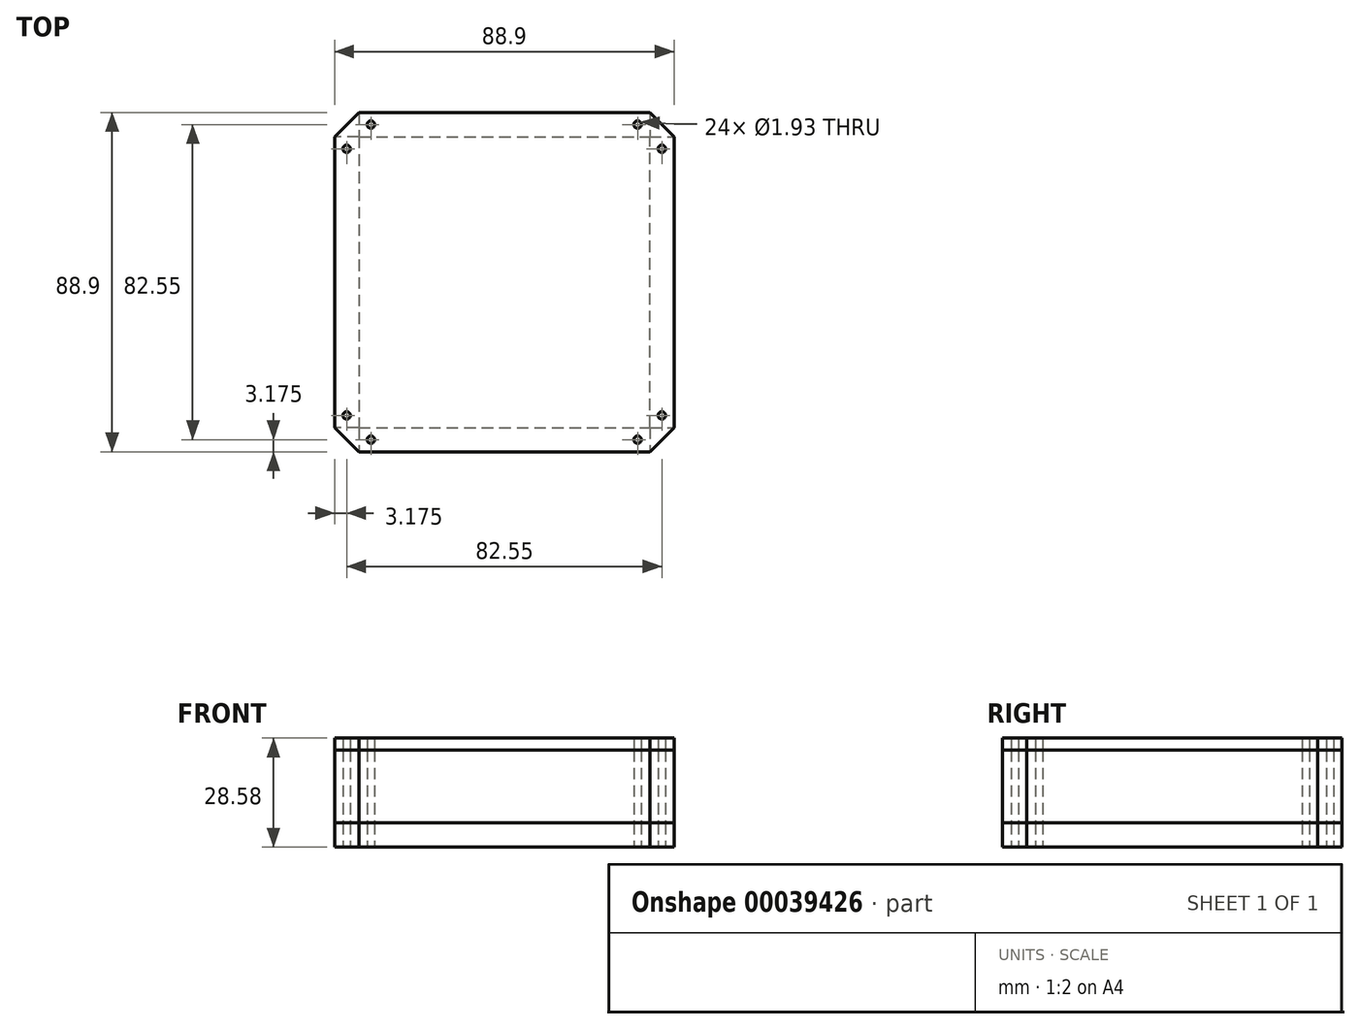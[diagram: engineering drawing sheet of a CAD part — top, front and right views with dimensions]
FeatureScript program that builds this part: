
annotation { "Feature Type Name" : "Feature", "Feature Type Description" : "" }
export const myFeature = defineFeature(function(context is Context, id is Id, definition is map)
    precondition{}
    {
        {
            var Q0;
            Q0=qCreatedBy(makeId("Top.planeOp"),FACE);
            var sketch = newSketch(context, id + "F0", { "sketchPlane" : qUnion([Q0])});
            skLineSegment(sketch, "E0.rect.bottom", {"start": v(-38.1, 44.45) * mm, "end": v(38.1, 44.45) * mm});
            skLineSegment(sketch, "E0.rect.top", {"start": v(-38.1, -44.45) * mm, "end": v(38.1, -44.45) * mm});
            skLineSegment(sketch, "E0.rect.left", {"start": v(-44.45, 38.1) * mm, "end": v(-44.45, -38.1) * mm});
            skLineSegment(sketch, "E0.rect.right", {"start": v(44.45, 38.1) * mm, "end": v(44.45, -38.1) * mm});
            skPoint(sketch, "E0.rect.middle", {"position": v(0, 0) * mm});
            skLineSegment(sketch, "E1", {"start": v(-44.45, 38.1) * mm, "end": v(-38.1, 44.45) * mm});
            skLineSegment(sketch, "E2", {"start": v(38.1, 44.45) * mm, "end": v(44.45, 38.1) * mm});
            skLineSegment(sketch, "E3", {"start": v(44.45, -38.1) * mm, "end": v(38.1, -44.45) * mm});
            skLineSegment(sketch, "E4", {"start": v(-38.1, -44.45) * mm, "end": v(-44.45, -38.1) * mm});
            skPoint(sketch, "E5.orphan", {"position": v(-44.45, 44.45) * mm});
            skPoint(sketch, "E6.orphan", {"position": v(44.45, 44.45) * mm});
            skPoint(sketch, "E7.orphan", {"position": v(44.45, -44.45) * mm});
            skPoint(sketch, "E8.orphan", {"position": v(-44.45, -44.45) * mm});
            skCircle(sketch, "E9", {"center": v(-34.93, 41.28) * mm, "radius": 0.97 * mm});
            skCircle(sketch, "E10", {"center": v(-41.28, 34.93) * mm, "radius": 0.97 * mm});
            skCircle(sketch, "E11", {"center": v(34.93, 41.28) * mm, "radius": 0.97 * mm});
            skCircle(sketch, "E12", {"center": v(41.28, 34.93) * mm, "radius": 0.97 * mm});
            skLineSegment(sketch, "E13", {"start": v(-16.26, 0) * mm, "end": v(10.9, 0) * mm});
            skCircle(sketch, "E14.MirrorC", {"center": v(-41.28, -34.93) * mm, "radius": 0.97 * mm});
            skCircle(sketch, "E15.MirrorC", {"center": v(-34.93, -41.28) * mm, "radius": 0.97 * mm});
            skCircle(sketch, "E16.MirrorC", {"center": v(34.93, -41.28) * mm, "radius": 0.97 * mm});
            skCircle(sketch, "E17.MirrorC", {"center": v(41.28, -34.93) * mm, "radius": 0.97 * mm});
            skSolve(sketch);
        }
        {
            var Q0;
            Q0 = qSketchRegion(id + "F0", true);
            extrude(context, id + "F1", {"entities" : qUnion([Q0]), "depth" : 6.35 * mm});
        }
        {
            var Q0;
            Q0=makeQuery(id+"F1.opExtrude","CAP_FACE",FACE,{"disambiguationData":[OSD([sQuery(id+"F0.wireOp",EDGE,"E0.rect.bottom"),sQuery(id+"F0.wireOp",EDGE,"E0.rect.top"),sQuery(id+"F0.wireOp",EDGE,"E0.rect.left"),sQuery(id+"F0.wireOp",EDGE,"E0.rect.right"),sQuery(id+"F0.wireOp",EDGE,"E1"),sQuery(id+"F0.wireOp",EDGE,"E2"),sQuery(id+"F0.wireOp",EDGE,"E3"),sQuery(id+"F0.wireOp",EDGE,"E4"),sQuery(id+"F0.wireOp",EDGE,"E9"),sQuery(id+"F0.wireOp",EDGE,"E10"),sQuery(id+"F0.wireOp",EDGE,"E11"),sQuery(id+"F0.wireOp",EDGE,"E12"),sQuery(id+"F0.wireOp",EDGE,"E14.MirrorC"),sQuery(id+"F0.wireOp",EDGE,"E15.MirrorC"),sQuery(id+"F0.wireOp",EDGE,"E16.MirrorC"),sQuery(id+"F0.wireOp",EDGE,"E17.MirrorC")])],"isStart":false});
            var sketch = newSketch(context, id + "F2", { "sketchPlane" : qUnion([Q0])});
            skLineSegment(sketch, "E18.bottom", {"start": v(-38.1, 44.45) * mm, "end": v(38.1, 44.45) * mm});
            skLineSegment(sketch, "E18.top", {"start": v(-38.1, 38.1) * mm, "end": v(38.1, 38.1) * mm});
            skLineSegment(sketch, "E18.left", {"start": v(-38.1, 44.45) * mm, "end": v(-38.1, 38.1) * mm});
            skLineSegment(sketch, "E18.right", {"start": v(38.1, 44.45) * mm, "end": v(38.1, 38.1) * mm});
            skLineSegment(sketch, "E19.bottom", {"start": v(-38.1, 38.1) * mm, "end": v(-44.45, 38.1) * mm});
            skLineSegment(sketch, "E19.top", {"start": v(-38.1, -38.1) * mm, "end": v(-44.45, -38.1) * mm});
            skLineSegment(sketch, "E19.left", {"start": v(-38.1, 38.1) * mm, "end": v(-38.1, -38.1) * mm});
            skLineSegment(sketch, "E19.right", {"start": v(-44.45, 38.1) * mm, "end": v(-44.45, -38.1) * mm});
            skLineSegment(sketch, "E20.bottom", {"start": v(-38.1, -38.1) * mm, "end": v(38.1, -38.1) * mm});
            skLineSegment(sketch, "E20.top", {"start": v(-38.1, -44.45) * mm, "end": v(38.1, -44.45) * mm});
            skLineSegment(sketch, "E20.left", {"start": v(-38.1, -38.1) * mm, "end": v(-38.1, -44.45) * mm});
            skLineSegment(sketch, "E20.right", {"start": v(38.1, -38.1) * mm, "end": v(38.1, -44.45) * mm});
            skLineSegment(sketch, "E21.bottom", {"start": v(38.1, -38.1) * mm, "end": v(44.45, -38.1) * mm});
            skLineSegment(sketch, "E21.top", {"start": v(38.1, 38.1) * mm, "end": v(44.45, 38.1) * mm});
            skLineSegment(sketch, "E21.left", {"start": v(38.1, -38.1) * mm, "end": v(38.1, 38.1) * mm});
            skLineSegment(sketch, "E21.right", {"start": v(44.45, -38.1) * mm, "end": v(44.45, 38.1) * mm});
            skCircle(sketch, "E22.0", {"center": v(-34.93, 41.28) * mm, "radius": 0.97 * mm});
            skCircle(sketch, "E23.0", {"center": v(34.93, 41.28) * mm, "radius": 0.97 * mm});
            skCircle(sketch, "E24.0", {"center": v(41.28, 34.93) * mm, "radius": 0.97 * mm});
            skCircle(sketch, "E25.0", {"center": v(-41.28, 34.93) * mm, "radius": 0.97 * mm});
            skCircle(sketch, "E26.0", {"center": v(-41.28, -34.93) * mm, "radius": 0.97 * mm});
            skCircle(sketch, "E27.0", {"center": v(-34.93, -41.28) * mm, "radius": 0.97 * mm});
            skCircle(sketch, "E28.0", {"center": v(34.93, -41.28) * mm, "radius": 0.97 * mm});
            skCircle(sketch, "E29.0", {"center": v(41.28, -34.93) * mm, "radius": 0.97 * mm});
            skSolve(sketch);
        }
        {
            var Q0;
            Q0=makeQuery(id+"F2.imprint","IMPRINT",FACE,{"disambiguationData":[TD([[makeQuery(id+"F2.imprint","IMPRINT",EDGE,{"derivedFrom":sQuery(id+"F2.wireOp",EDGE,"E18.bottom")}),-1.0]])]});
            var Q1;
            Q1=makeQuery(id+"F2.imprint","IMPRINT",FACE,{"disambiguationData":[TD([[makeQuery(id+"F2.imprint","IMPRINT",EDGE,{"derivedFrom":sQuery(id+"F2.wireOp",EDGE,"E19.bottom")}),1.0]])]});
            var Q2;
            Q2=makeQuery(id+"F2.imprint","IMPRINT",FACE,{"disambiguationData":[TD([[makeQuery(id+"F2.imprint","IMPRINT",EDGE,{"derivedFrom":sQuery(id+"F2.wireOp",EDGE,"E20.bottom")}),-1.0]])]});
            var Q3;
            Q3=makeQuery(id+"F2.imprint","IMPRINT",FACE,{"disambiguationData":[TD([[makeQuery(id+"F2.imprint","IMPRINT",EDGE,{"derivedFrom":sQuery(id+"F2.wireOp",EDGE,"E21.bottom")}),1.0]])]});
            extrude(context, id + "F3", {"entities" : qUnion([Q0, Q1, Q2, Q3]), "depth" : 19.05 * mm});
        }
        {
            var Q0;
            Q0=makeQuery(id+"F3.opExtrude","CAP_FACE",FACE,{"disambiguationData":[OSD([sQuery(id+"F2.wireOp",EDGE,"E18.bottom"),sQuery(id+"F2.wireOp",EDGE,"E18.top"),sQuery(id+"F2.wireOp",EDGE,"E18.left"),sQuery(id+"F2.wireOp",EDGE,"E18.right"),sQuery(id+"F2.wireOp",EDGE,"E22.0"),sQuery(id+"F2.wireOp",EDGE,"E23.0")])],"isStart":false});
            var sketch = newSketch(context, id + "F4", { "sketchPlane" : qUnion([Q0])});
            skLineSegment(sketch, "E30.0.0", {"start": v(38.1, 44.45) * mm, "end": v(-38.1, 44.45) * mm});
            skLineSegment(sketch, "E30.0.1", {"start": v(-38.1, 44.45) * mm, "end": v(-44.45, 38.1) * mm});
            skLineSegment(sketch, "E30.0.2", {"start": v(-44.45, 38.1) * mm, "end": v(-44.45, -38.1) * mm});
            skLineSegment(sketch, "E30.0.3", {"start": v(-44.45, -38.1) * mm, "end": v(-38.1, -44.45) * mm});
            skLineSegment(sketch, "E30.0.4", {"start": v(-38.1, -44.45) * mm, "end": v(38.1, -44.45) * mm});
            skLineSegment(sketch, "E30.0.5", {"start": v(38.1, -44.45) * mm, "end": v(44.45, -38.1) * mm});
            skLineSegment(sketch, "E30.0.6", {"start": v(44.45, -38.1) * mm, "end": v(44.45, 38.1) * mm});
            skLineSegment(sketch, "E30.0.7", {"start": v(44.45, 38.1) * mm, "end": v(38.1, 44.45) * mm});
            skCircle(sketch, "E31.0", {"center": v(-34.93, 41.28) * mm, "radius": 0.97 * mm});
            skCircle(sketch, "E32.0", {"center": v(-41.28, 34.93) * mm, "radius": 0.97 * mm});
            skCircle(sketch, "E33.0", {"center": v(34.93, 41.28) * mm, "radius": 0.97 * mm});
            skCircle(sketch, "E34.0", {"center": v(41.28, 34.93) * mm, "radius": 0.97 * mm});
            skCircle(sketch, "E35.0", {"center": v(41.28, -34.93) * mm, "radius": 0.97 * mm});
            skCircle(sketch, "E36.0", {"center": v(34.93, -41.28) * mm, "radius": 0.97 * mm});
            skCircle(sketch, "E37.0", {"center": v(-34.93, -41.28) * mm, "radius": 0.97 * mm});
            skCircle(sketch, "E38.0", {"center": v(-41.28, -34.93) * mm, "radius": 0.97 * mm});
            skSolve(sketch);
        }
        {
            var Q0;
            Q0 = qSketchRegion(id + "F4", true);
            extrude(context, id + "F5", {"entities" : qUnion([Q0]), "depth" : 3.17 * mm});
        }
    });
